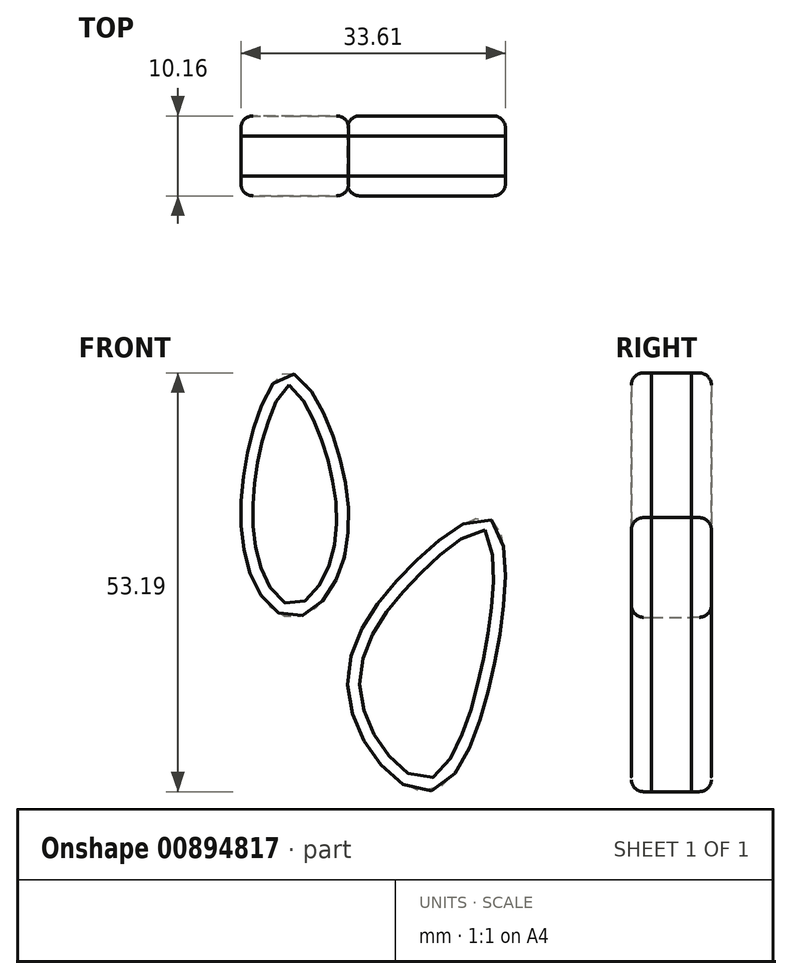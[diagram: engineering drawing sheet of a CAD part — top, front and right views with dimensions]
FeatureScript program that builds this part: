
annotation { "Feature Type Name" : "Feature", "Feature Type Description" : "" }
export const myFeature = defineFeature(function(context is Context, id is Id, definition is map)
    precondition{}
    {
        {
            var Q0;
            Q0=qCreatedBy(makeId("Front.planeOp"),FACE);
            var sketch = newSketch(context, id + "F0", { "sketchPlane" : qUnion([Q0])});
            skLineSegment(sketch, "E0", {"start": v(-12.43, 147.36) * mm, "end": v(-12.43, 694.5) * mm});
            skLineSegment(sketch, "E1", {"start": v(18.75, 182.02) * mm, "end": v(18.75, 802.28) * mm});
            skFitSpline(sketch, "E2", {"points": [v(18.75, 802.28) * mm, v(14.92, 802.28) * mm, v(0, 769.63) * mm, v(-9.09, 710.4) * mm, v(-12.43, 694.5) * mm], "startDerivative": vector(-36.41, 12.36) * mm, "endDerivative": vector(-16.8, -63.7) * mm});
            skLineSegment(sketch, "E3", {"start": v(-12.43, 147.36) * mm, "end": v(-12.43, 112.48) * mm});
            skLineSegment(sketch, "E4", {"start": v(18.75, 182.02) * mm, "end": v(18.75, 112.48) * mm});
            skLineSegment(sketch, "E5", {"start": v(18.75, 112.48) * mm, "end": v(-12.43, 112.48) * mm});
            skFitSpline(sketch, "E6", {"points": [v(-12.97, -121.38) * mm, v(-16.97, -125) * mm, v(-19.15, -144.62) * mm, v(-12.97, -152.25) * mm, v(-6.07, -141.35) * mm, v(-12.97, -121.38) * mm]});
            skFitSpline(sketch, "E7", {"points": [v(12.1, -139.9) * mm, v(12.46, -158.43) * mm, v(3.74, -174.4) * mm, v(-6.07, -162.06) * mm, v(2.65, -144.99) * mm, v(12.1, -139.9) * mm]});
            skSolve(sketch);
        }
        {
            var Q0;
            Q0=makeQuery(id+"F0.imprint","IMPRINT",FACE,{"disambiguationData":[TD([[makeQuery(id+"F0.imprint","IMPRINT",EDGE,{"derivedFrom":sQuery(id+"F0.wireOp",EDGE,"E7")}),-1.0]])]});
            var Q1;
            Q1=makeQuery(id+"F0.imprint","IMPRINT",FACE,{"disambiguationData":[TD([[makeQuery(id+"F0.imprint","IMPRINT",EDGE,{"derivedFrom":sQuery(id+"F0.wireOp",EDGE,"E6")}),1.0]])]});
            extrude(context, id + "F1", {"entities" : qUnion([Q0, Q1]), "depth" : 2.54 * mm, "offsetDistance" : 25.4 * mm});
        }
        {
            var Q0;
            Q0=makeQuery(id+"F1.opExtrude","CAP_FACE",FACE,{"disambiguationData":[OSD([sQuery(id+"F0.wireOp",EDGE,"E7")])],"isStart":true});
            extrude(context, id + "F2", {"entities" : qUnion([Q0]), "operationType" : NewBodyOperationType.ADD, "depth" : 2.54 * mm, "offsetDistance" : 25.4 * mm});
        }
        {
            var Q0;
            Q0=makeQuery(id+"F1.opExtrude","CAP_FACE",FACE,{"disambiguationData":[OSD([sQuery(id+"F0.wireOp",EDGE,"E6")])],"isStart":true});
            extrude(context, id + "F3", {"entities" : qUnion([Q0]), "operationType" : NewBodyOperationType.ADD, "depth" : 2.54 * mm, "offsetDistance" : 25.4 * mm});
        }
        {
            var Q0;
            Q0=makeQuery(id+"F3.opExtrude","CAP_FACE",FACE,{"disambiguationData":[OSD([sQuery(id+"F0.wireOp",EDGE,"E6")])],"isStart":false});
            var Q1;
            Q1=makeQuery(id+"F2.opExtrude","CAP_FACE",FACE,{"disambiguationData":[OSD([sQuery(id+"F0.wireOp",EDGE,"E7")])],"isStart":false});
            extrude(context, id + "F4", {"entities" : qUnion([Q0, Q1]), "depth" : 2.54 * mm, "offsetDistance" : 25.4 * mm});
        }
        {
            var Q0;
            Q0=makeQuery(id+"F1.opExtrude","CAP_FACE",FACE,{"disambiguationData":[OSD([sQuery(id+"F0.wireOp",EDGE,"E6")])],"isStart":false});
            var Q1;
            Q1=makeQuery(id+"F1.opExtrude","CAP_FACE",FACE,{"disambiguationData":[OSD([sQuery(id+"F0.wireOp",EDGE,"E7")])],"isStart":false});
            extrude(context, id + "F5", {"entities" : qUnion([Q0, Q1]), "depth" : 2.54 * mm, "offsetDistance" : 25.4 * mm});
        }
        {
            var Q0;
            Q0=makeQuery(id+"F5.opExtrude","CAP_FACE",FACE,{"disambiguationData":[OSD([sQuery(id+"F0.wireOp",EDGE,"E7")])],"isStart":false});
            var Q1;
            Q1=makeQuery(id+"F5.opExtrude","CAP_FACE",FACE,{"disambiguationData":[OSD([sQuery(id+"F0.wireOp",EDGE,"E6")])],"isStart":false});
            var Q2;
            Q2=makeQuery(id+"F4.opExtrude","CAP_FACE",FACE,{"disambiguationData":[OSD([sQuery(id+"F0.wireOp",EDGE,"E6")])],"isStart":false});
            var Q3;
            Q3=makeQuery(id+"F4.opExtrude","CAP_FACE",FACE,{"disambiguationData":[OSD([sQuery(id+"F0.wireOp",EDGE,"E7")])],"isStart":false});
            fillet(context, id + "F6", {"entities" : qUnion([Q0, Q1, Q2, Q3]), "radius" : 1.52 * mm, "tangentPropagation" : true, "allowEdgeOverflow" : false});
        }
    });
